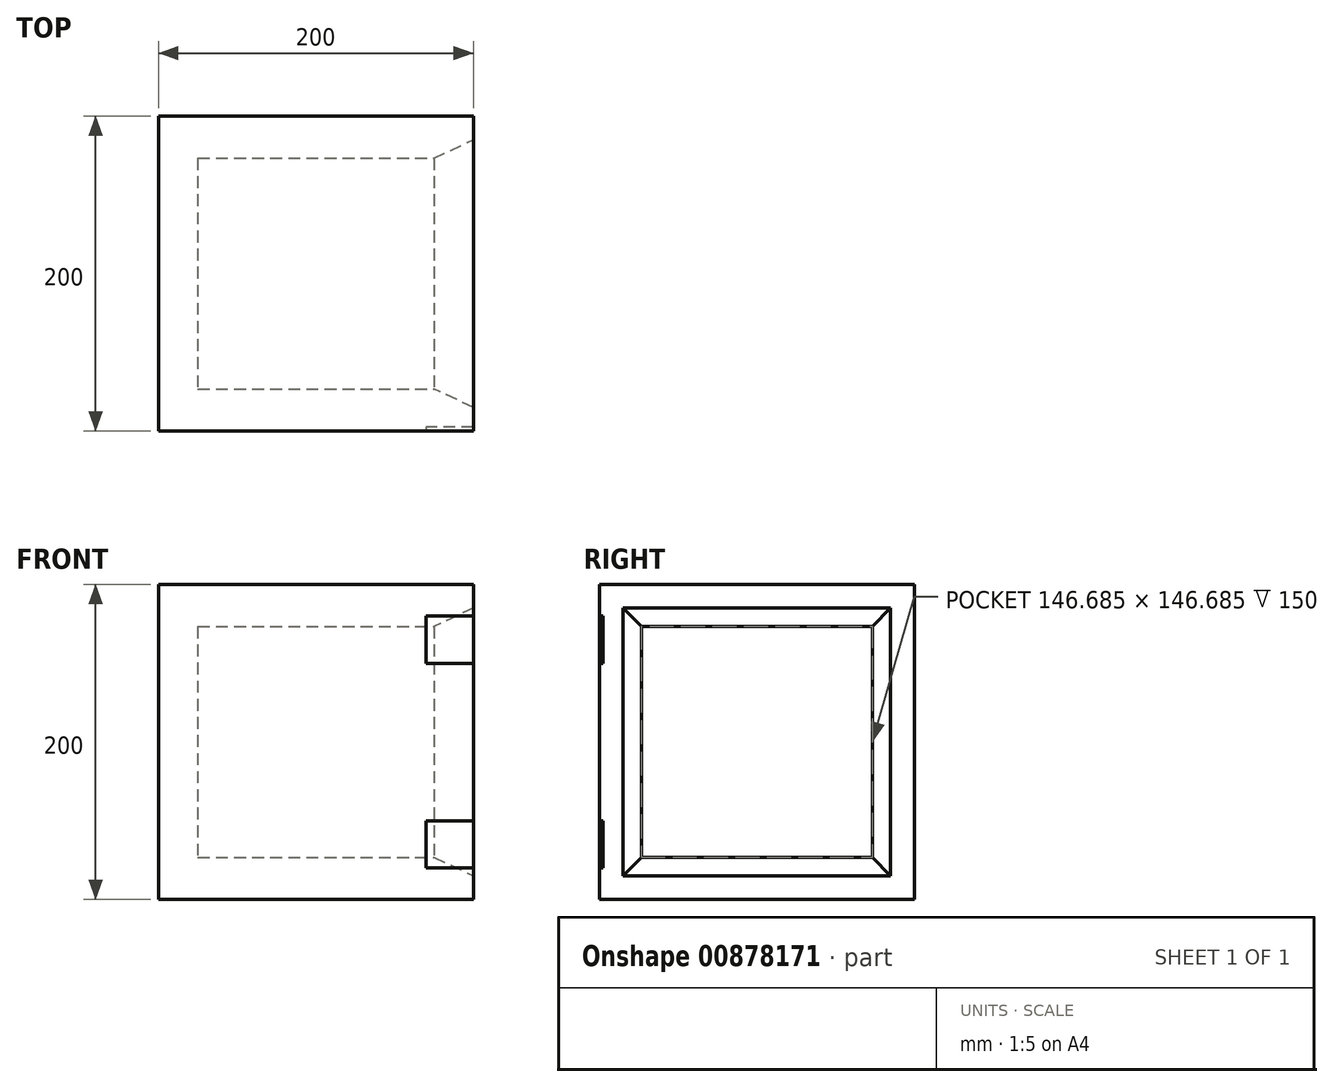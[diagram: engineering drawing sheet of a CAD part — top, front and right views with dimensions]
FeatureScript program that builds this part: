
annotation { "Feature Type Name" : "Feature", "Feature Type Description" : "" }
export const myFeature = defineFeature(function(context is Context, id is Id, definition is map)
    precondition{}
    {
        {
            var Q0;
            Q0=qCreatedBy(makeId("Top.planeOp"),FACE);
            var sketch = newSketch(context, id + "F0", { "sketchPlane" : qUnion([Q0])});
            skLineSegment(sketch, "E0.bottom", {"start": v(0, 0) * mm, "end": v(200, 0) * mm});
            skLineSegment(sketch, "E0.top", {"start": v(0, 200) * mm, "end": v(200, 200) * mm});
            skLineSegment(sketch, "E0.left", {"start": v(0, 0) * mm, "end": v(0, 200) * mm});
            skLineSegment(sketch, "E0.right", {"start": v(200, 0) * mm, "end": v(200, 200) * mm});
            skSolve(sketch);
        }
        {
            var Q0;
            Q0 = qSketchRegion(id + "F0", true);
            extrude(context, id + "F1", {"entities" : qUnion([Q0]), "depth" : 200 * mm, "offsetDistance" : 25 * mm});
        }
        {
            var Q0;
            Q0=makeQuery(id+"F1.opExtrude","SWEPT_FACE",FACE,{"disambiguationData":[OSD([sQuery(id+"F0.wireOp",EDGE,"E0.right")])]});
            var sketch = newSketch(context, id + "F2", { "sketchPlane" : qUnion([Q0])});
            skLineSegment(sketch, "E1.bottom", {"start": v(15, 185) * mm, "end": v(185, 185) * mm});
            skLineSegment(sketch, "E1.top", {"start": v(15, 15) * mm, "end": v(185, 15) * mm});
            skLineSegment(sketch, "E1.left", {"start": v(15, 185) * mm, "end": v(15, 15) * mm});
            skLineSegment(sketch, "E1.right", {"start": v(185, 185) * mm, "end": v(185, 15) * mm});
            skSolve(sketch);
        }
        {
            var Q0;
            Q0=makeQuery(id+"F2.imprint","IMPRINT",FACE,{"disambiguationData":[TD([[makeQuery(id+"F2.imprint","IMPRINT",EDGE,{"derivedFrom":sQuery(id+"F2.wireOp",EDGE,"E1.bottom")}),-1.0]])]});
            extrude(context, id + "F3", {"entities" : qUnion([Q0]), "operationType" : NewBodyOperationType.REMOVE, "oppositeDirection" : true, "depth" : 25 * mm, "offsetDistance" : 25 * mm, "hasDraft" : true, "draftAngle" : 25 * degree, "draftPullDirection" : true});
        }
        {
            var Q0;
            Q0=makeQuery(id+"F3.boolean.opBoolean","COPY",FACE,{"derivedFrom":makeQuery(id+"F3.opExtrude","CAP_FACE",FACE,{"disambiguationData":[OSD([sQuery(id+"F2.wireOp",EDGE,"E1.bottom"),sQuery(id+"F2.wireOp",EDGE,"E1.top"),sQuery(id+"F2.wireOp",EDGE,"E1.left"),sQuery(id+"F2.wireOp",EDGE,"E1.right")])],"isStart":false})});
            var sketch = newSketch(context, id + "F4", { "sketchPlane" : qUnion([Q0])});
            skLineSegment(sketch, "E2.bottom", {"start": v(173.34, 173.34) * mm, "end": v(26.66, 173.34) * mm});
            skLineSegment(sketch, "E2.top", {"start": v(173.34, 26.66) * mm, "end": v(26.66, 26.66) * mm});
            skLineSegment(sketch, "E2.left", {"start": v(173.34, 173.34) * mm, "end": v(173.34, 26.66) * mm});
            skLineSegment(sketch, "E2.right", {"start": v(26.66, 173.34) * mm, "end": v(26.66, 26.66) * mm});
            skSolve(sketch);
        }
        {
            var Q0;
            Q0=makeQuery(id+"F4.imprint","IMPRINT",FACE,{"disambiguationData":[TD([[makeQuery(id+"F4.imprint","IMPRINT",EDGE,{"derivedFrom":sQuery(id+"F4.wireOp",EDGE,"E2.bottom")}),-1.0]])]});
            extrude(context, id + "F5", {"entities" : qUnion([Q0]), "operationType" : NewBodyOperationType.REMOVE, "oppositeDirection" : true, "depth" : 150 * mm, "offsetDistance" : 25 * mm});
        }
        {
            var Q0;
            Q0=makeQuery(id+"F1.opExtrude","SWEPT_FACE",FACE,{"disambiguationData":[OSD([sQuery(id+"F0.wireOp",EDGE,"E0.bottom")])]});
            var sketch = newSketch(context, id + "F6", { "sketchPlane" : qUnion([Q0])});
            skLineSegment(sketch, "E3.bottom", {"start": v(200, 20) * mm, "end": v(170, 20) * mm});
            skLineSegment(sketch, "E3.top", {"start": v(200, 50) * mm, "end": v(170, 50) * mm});
            skLineSegment(sketch, "E3.left", {"start": v(200, 20) * mm, "end": v(200, 50) * mm});
            skLineSegment(sketch, "E3.right", {"start": v(170, 20) * mm, "end": v(170, 50) * mm});
            skLineSegment(sketch, "E4.bottom", {"start": v(200, 150) * mm, "end": v(170, 150) * mm});
            skLineSegment(sketch, "E4.top", {"start": v(200, 180) * mm, "end": v(170, 180) * mm});
            skLineSegment(sketch, "E4.left", {"start": v(200, 150) * mm, "end": v(200, 180) * mm});
            skLineSegment(sketch, "E4.right", {"start": v(170, 150) * mm, "end": v(170, 180) * mm});
            skSolve(sketch);
        }
        {
            var Q0;
            Q0=makeQuery(id+"F6.imprint","IMPRINT",FACE,{"disambiguationData":[TD([[makeQuery(id+"F6.imprint","IMPRINT",EDGE,{"derivedFrom":sQuery(id+"F6.wireOp",EDGE,"E4.bottom")}),-1.0]])]});
            var Q1;
            Q1=makeQuery(id+"F6.imprint","IMPRINT",FACE,{"disambiguationData":[TD([[makeQuery(id+"F6.imprint","IMPRINT",EDGE,{"derivedFrom":sQuery(id+"F6.wireOp",EDGE,"E3.bottom")}),-1.0]])]});
            extrude(context, id + "F7", {"entities" : qUnion([Q0, Q1]), "operationType" : NewBodyOperationType.REMOVE, "oppositeDirection" : true, "depth" : 2.5 * mm, "offsetDistance" : 25 * mm});
        }
    });
